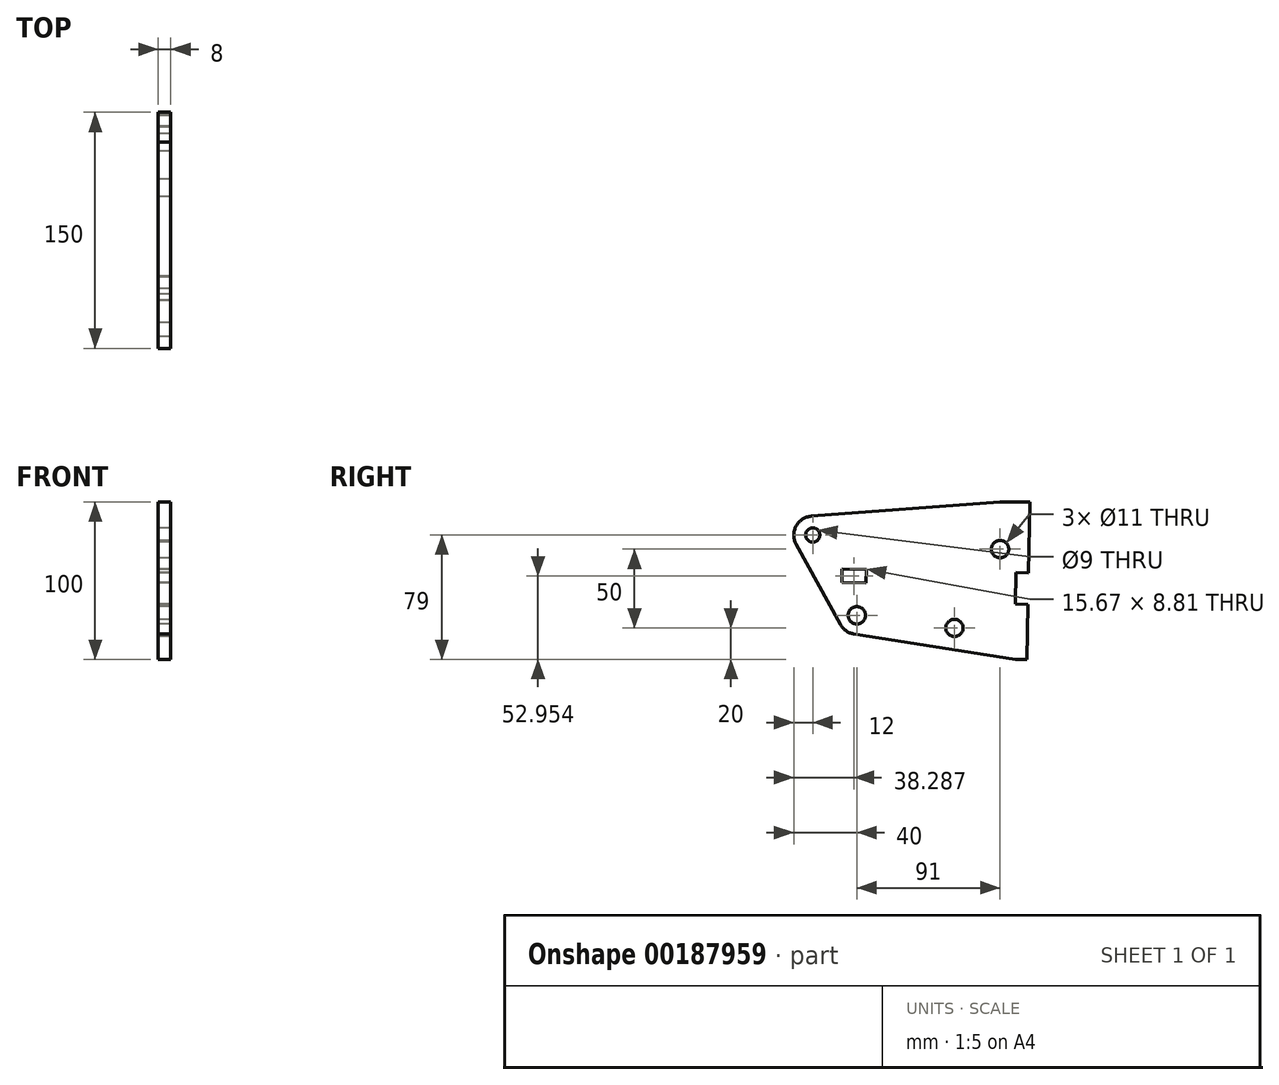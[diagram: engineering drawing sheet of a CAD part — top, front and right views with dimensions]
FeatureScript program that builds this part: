
annotation { "Feature Type Name" : "Feature", "Feature Type Description" : "" }
export const myFeature = defineFeature(function(context is Context, id is Id, definition is map)
    precondition{}
    {
        {
            var Q0;
            Q0=qCreatedBy(makeId("Right.planeOp"),FACE);
            var sketch = newSketch(context, id + "F0", { "sketchPlane" : qUnion([Q0])});
            skCircle(sketch, "E0", {"center": v(0, 0) * mm, "radius": 5.5 * mm});
            skCircle(sketch, "E1", {"center": v(-119, 9) * mm, "radius": 4.5 * mm});
            skCircle(sketch, "E2", {"center": v(-29, -50) * mm, "radius": 5.5 * mm});
            skCircle(sketch, "E3", {"center": v(-91, -42) * mm, "radius": 5.5 * mm});
            skLineSegment(sketch, "E4", {"start": v(25, 30) * mm, "end": v(0, 30) * mm});
            skLineSegment(sketch, "E5", {"start": v(9.78, -70) * mm, "end": v(25, -70) * mm});
            skArc(sketch, "E6", {"start": v(-119.9, 20.97) * mm, "mid": v(-129.57, 14.68) * mm, "end": v(-129.48, 3.15) * mm});
            skLineSegment(sketch, "E7", {"start": v(0, 30) * mm, "end": v(-119.9, 20.97) * mm});
            skArc(sketch, "E8", {"start": v(-101.52, -47.78) * mm, "mid": v(-97.96, -51.77) * mm, "end": v(-93.03, -53.83) * mm});
            skLineSegment(sketch, "E9", {"start": v(-129.56, 3.3) * mm, "end": v(-101.52, -47.78) * mm});
            skLineSegment(sketch, "E10", {"start": v(-93.03, -53.83) * mm, "end": v(9.78, -70) * mm});
            skLineSegment(sketch, "E11", {"start": v(19.23, 41.6) * mm, "end": v(16.86, -76.8) * mm});
            skPoint(sketch, "E12", {"position": v(19, 30) * mm});
            skPoint(sketch, "E13", {"position": v(17, -70) * mm});
            skLineSegment(sketch, "E14", {"start": v(17.7, -35) * mm, "end": v(9.7, -34.85) * mm});
            skLineSegment(sketch, "E15", {"start": v(9.7, -34.85) * mm, "end": v(10.1, -14.85) * mm});
            skLineSegment(sketch, "E16", {"start": v(10.1, -14.85) * mm, "end": v(18.1, -15.01) * mm});
            skLineSegment(sketch, "E17", {"start": v(18.1, -15.01) * mm, "end": v(-112.73, -12.4) * mm});
            skLineSegment(sketch, "E18", {"start": v(-84.88, -12.95) * mm, "end": v(-85.05, -21.45) * mm});
            skLineSegment(sketch, "E19", {"start": v(-85.05, -21.45) * mm, "end": v(-100.55, -21.14) * mm});
            skLineSegment(sketch, "E20", {"start": v(-100.55, -21.14) * mm, "end": v(-100.38, -12.64) * mm});
            skSolve(sketch);
        }
        {
            var Q0;
            Q0=makeQuery(id+"F0.imprint","IMPRINT",FACE,{"disambiguationData":[TD([[makeQuery(id+"F0.imprint","IMPRINT",EDGE,{"derivedFrom":sQuery(id+"F0.wireOp",EDGE,"E0")}),-1.0]])]});
            extrude(context, id + "F1", {"entities" : qUnion([Q0]), "depth" : 8 * mm});
        }
    });
